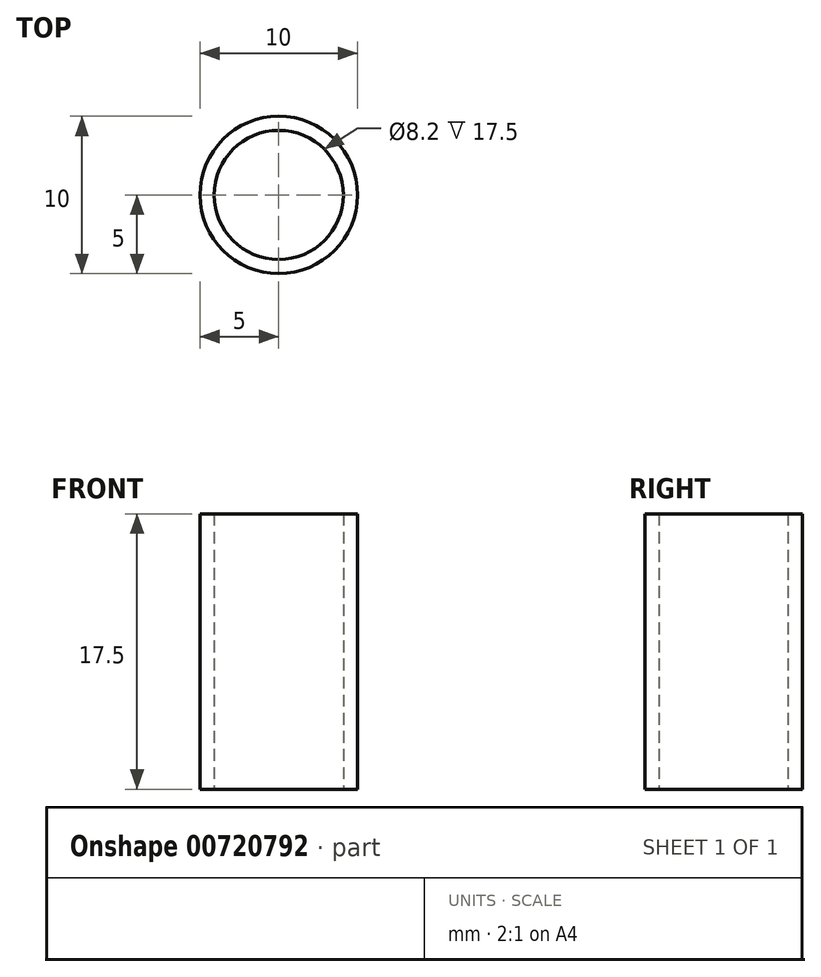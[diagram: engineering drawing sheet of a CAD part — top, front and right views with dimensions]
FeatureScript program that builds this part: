
annotation { "Feature Type Name" : "Feature", "Feature Type Description" : "" }
export const myFeature = defineFeature(function(context is Context, id is Id, definition is map)
    precondition{}
    {
        {
            var Q0;
            Q0=qCreatedBy(makeId("Top.planeOp"),FACE);
            var sketch = newSketch(context, id + "F0", { "sketchPlane" : qUnion([Q0])});
            skCircle(sketch, "E0", {"center": v(0, 0) * mm, "radius": 4.1 * mm});
            skCircle(sketch, "E1", {"center": v(0, 0) * mm, "radius": 5 * mm});
            skSolve(sketch);
        }
        {
            var Q0;
            Q0=makeQuery(id+"F0.imprint","IMPRINT",FACE,{"disambiguationData":[TD([[makeQuery(id+"F0.imprint","IMPRINT",EDGE,{"derivedFrom":sQuery(id+"F0.wireOp",EDGE,"E0")}),-1.0]])]});
            extrude(context, id + "F1", {"entities" : qUnion([Q0]), "depth" : 17.5 * mm, "offsetDistance" : 25 * mm});
        }
    });
